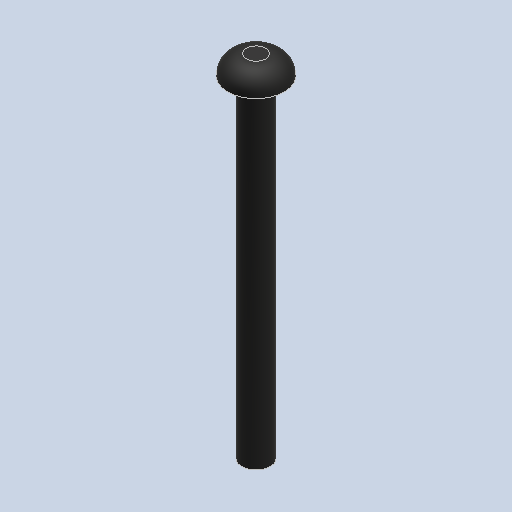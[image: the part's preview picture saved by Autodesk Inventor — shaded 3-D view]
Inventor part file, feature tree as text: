
AUTODESK INVENTOR PART (.ipt)
format: ipt  version: 2023 (Build 270158030, 158C)  size: 242,688 bytes
history: native  units: mm
features: extrude x2, sketch x2, other x1, fillet x1
ambient origin geometry x8: Origin, YZ Plane, XZ Plane, XY Plane, X Axis, Y Axis, Z Axis, Center Point
bodies: Body1 (feature_tree)
feature tree (6):
  other  "ソリッド1"
  extrude  "押し出し1"  Depth=3.0mm
  extrude  "押し出し2"  Depth=35.0mm TaperAngle=0.0deg
  fillet  "フィレット1"  Radius=6.0mm
  sketch  "スケッチ1"
  sketch  "スケッチ2"
